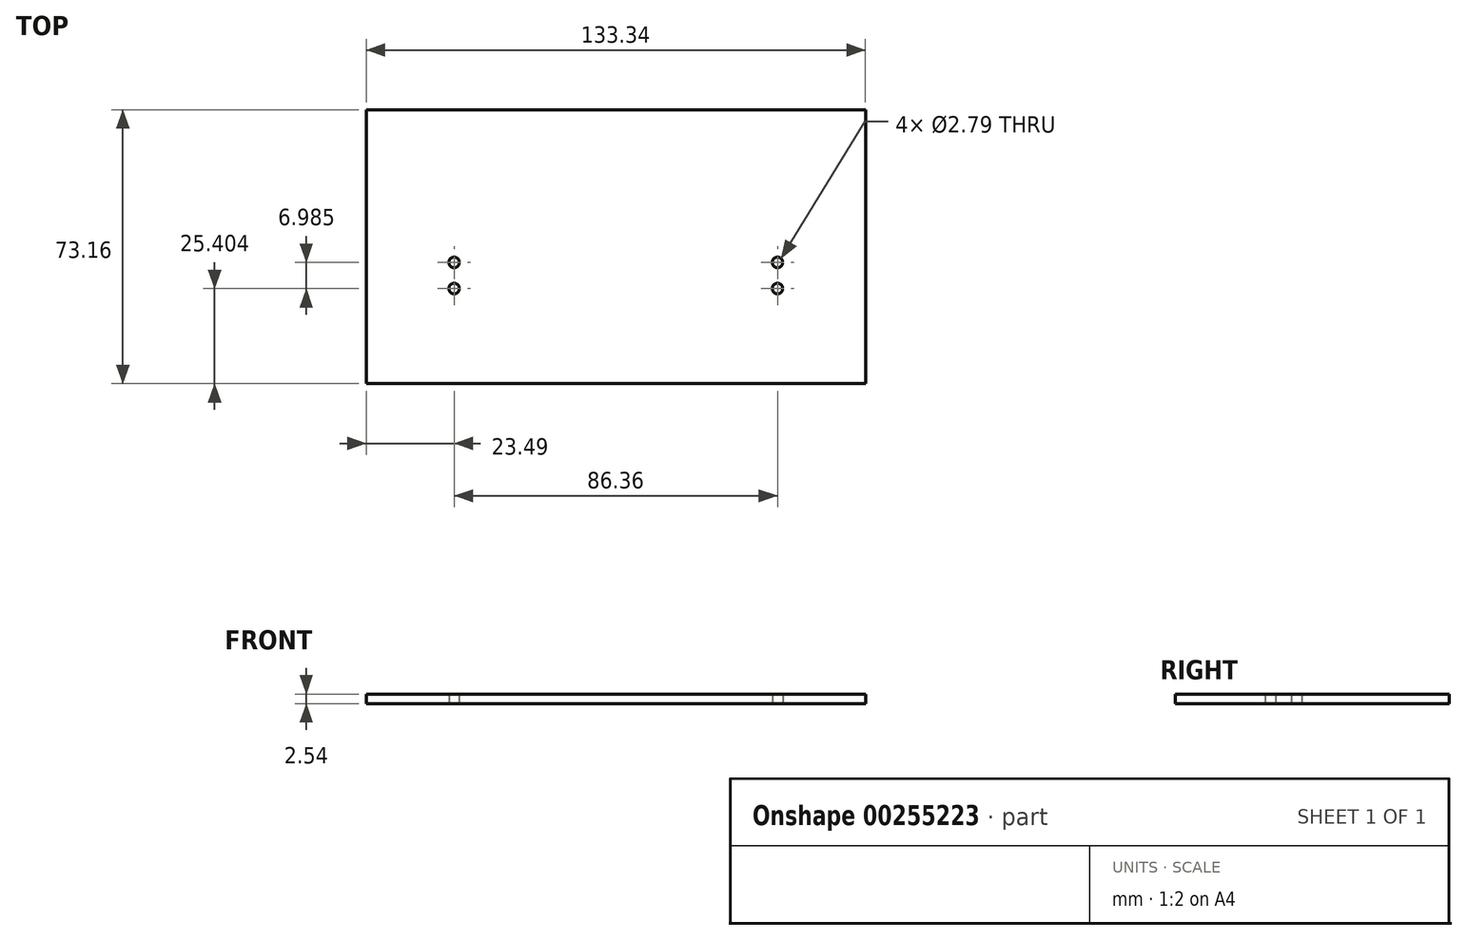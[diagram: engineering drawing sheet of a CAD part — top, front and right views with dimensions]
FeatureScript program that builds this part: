
annotation { "Feature Type Name" : "Feature", "Feature Type Description" : "" }
export const myFeature = defineFeature(function(context is Context, id is Id, definition is map)
    precondition{}
    {
        {
            var Q0;
            Q0=qCreatedBy(makeId("Top.planeOp"),FACE);
            var sketch = newSketch(context, id + "F0", { "sketchPlane" : qUnion([Q0])});
            skLineSegment(sketch, "E0.bottom", {"start": v(66.68, 36.58) * mm, "end": v(-66.68, 36.58) * mm});
            skLineSegment(sketch, "E0.top", {"start": v(66.68, -36.58) * mm, "end": v(-66.68, -36.58) * mm});
            skLineSegment(sketch, "E0.left", {"start": v(66.68, 36.58) * mm, "end": v(66.68, -36.58) * mm});
            skLineSegment(sketch, "E0.right", {"start": v(-66.68, 36.58) * mm, "end": v(-66.68, -36.58) * mm});
            skPoint(sketch, "E0.middle", {"position": v(0, 0) * mm});
            skLineSegment(sketch, "E1.0", {"start": v(69.22, 39.12) * mm, "end": v(69.22, -39.12) * mm});
            skLineSegment(sketch, "E1.1", {"start": v(69.22, 39.12) * mm, "end": v(-69.22, 39.12) * mm});
            skLineSegment(sketch, "E1.2", {"start": v(-69.22, 39.12) * mm, "end": v(-69.22, -39.12) * mm});
            skLineSegment(sketch, "E1.3", {"start": v(69.22, -39.12) * mm, "end": v(-69.22, -39.12) * mm});
            skLineSegment(sketch, "E2.bottom", {"start": v(43.18, -4.2) * mm, "end": v(-43.18, -4.2) * mm, "construction": true});
            skLineSegment(sketch, "E2.top", {"start": v(43.18, -11.18) * mm, "end": v(-43.18, -11.18) * mm, "construction": true});
            skLineSegment(sketch, "E2.left", {"start": v(43.18, -4.2) * mm, "end": v(43.18, -11.18) * mm, "construction": true});
            skLineSegment(sketch, "E2.right", {"start": v(-43.18, -4.2) * mm, "end": v(-43.18, -11.18) * mm, "construction": true});
            skPoint(sketch, "E2.middle", {"position": v(0, -7.68) * mm});
            skCircle(sketch, "E3", {"center": v(-43.18, -4.2) * mm, "radius": 1.4 * mm});
            skCircle(sketch, "E4", {"center": v(43.18, -4.2) * mm, "radius": 1.4 * mm});
            skCircle(sketch, "E5", {"center": v(43.18, -11.18) * mm, "radius": 1.4 * mm});
            skCircle(sketch, "E6", {"center": v(-43.18, -11.18) * mm, "radius": 1.4 * mm});
            skSolve(sketch);
        }
        {
            var Q0;
            Q0=makeQuery(id+"F0.imprint","IMPRINT",FACE,{"disambiguationData":[TD([[makeQuery(id+"F0.imprint","IMPRINT",EDGE,{"derivedFrom":sQuery(id+"F0.wireOp",EDGE,"E0.bottom")}),1.0]])]});
            extrude(context, id + "F1", {"entities" : qUnion([Q0]), "depth" : 2.54 * mm});
        }
    });
